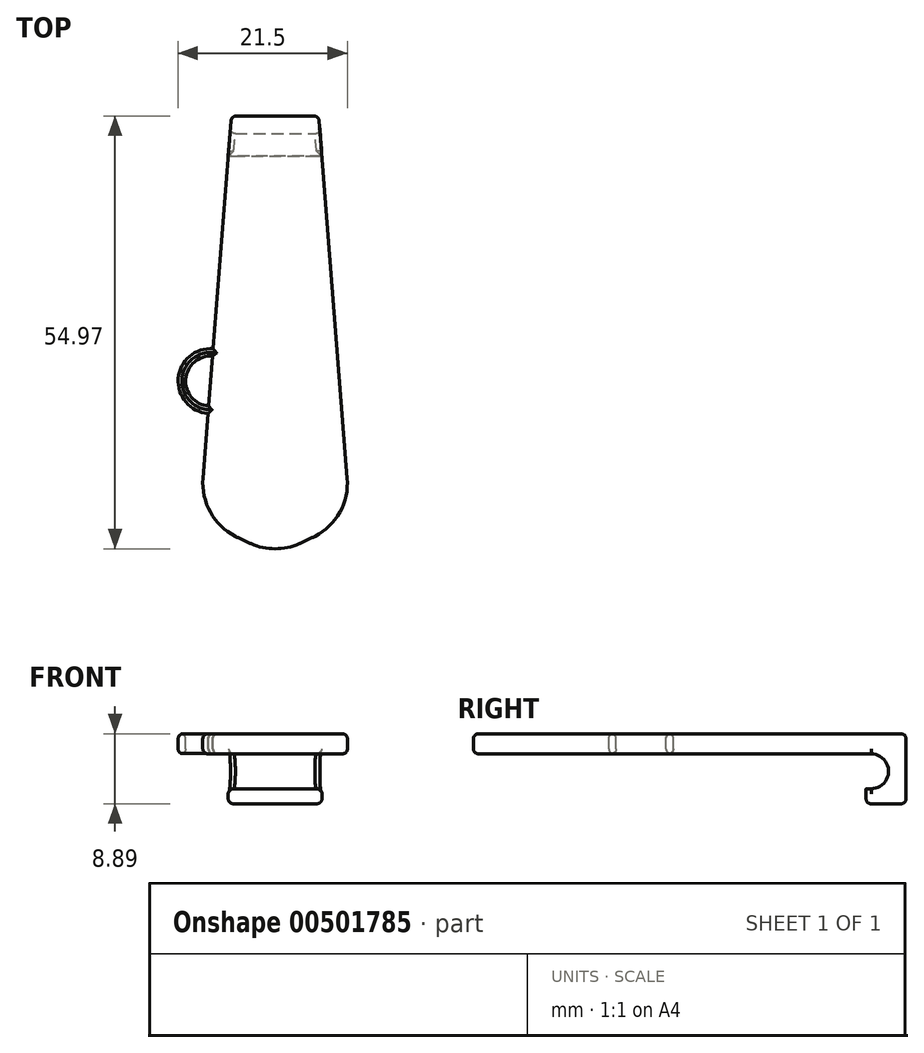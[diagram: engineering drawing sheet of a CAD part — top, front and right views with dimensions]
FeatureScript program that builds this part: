
annotation { "Feature Type Name" : "Feature", "Feature Type Description" : "" }
export const myFeature = defineFeature(function(context is Context, id is Id, definition is map)
    precondition{}
    {
        {
            var Q0;
            Q0=qCreatedBy(makeId("Top.planeOp"),FACE);
            var sketch = newSketch(context, id + "F0", { "sketchPlane" : qUnion([Q0])});
            skLineSegment(sketch, "E0", {"start": v(-9.52, -20.54) * mm, "end": v(-5.56, 30.1) * mm});
            skLineSegment(sketch, "E1", {"start": v(-5.56, 30.1) * mm, "end": v(0, 30.1) * mm});
            skArc(sketch, "E2", {"start": v(-9.52, -20.54) * mm, "mid": v(-4.94, -23.32) * mm, "end": v(0, -25.4) * mm});
            skLineSegment(sketch, "E3", {"start": v(0, 30.1) * mm, "end": v(0, -25.4) * mm});
            skSolve(sketch);
        }
        {
            var Q0;
            Q0=makeQuery(id+"F0.imprint","IMPRINT",FACE,{"disambiguationData":[TD([[makeQuery(id+"F0.imprint","IMPRINT",EDGE,{"derivedFrom":sQuery(id+"F0.wireOp",EDGE,"E0")}),-1.0]])]});
            extrude(context, id + "F1", {"entities" : qUnion([Q0]), "depth" : 2.54 * mm});
        }
        {
            var Q0;
            Q0=makeQuery(id+"F1.opExtrude","SWEPT_BODY",BODY,{"disambiguationData":[OSD([sQuery(id+"F0.wireOp",EDGE,"E0"),sQuery(id+"F0.wireOp",EDGE,"E1"),sQuery(id+"F0.wireOp",EDGE,"E2"),sQuery(id+"F0.wireOp",EDGE,"E3")])]});
            var Q1;
            Q1=qCreatedBy(makeId("Right.planeOp"),FACE);
            mirror(context, id + "F2", {"operationType" : NewBodyOperationType.ADD, "entities" : qUnion([Q0]), "mirrorPlane" : qUnion([Q1])});
        }
        {
            var Q0;
            {var subQ0=makeQuery(id+"F1.opExtrude","CAP_FACE",FACE,{"disambiguationData":[OSD([sQuery(id+"F0.wireOp",EDGE,"E0"),sQuery(id+"F0.wireOp",EDGE,"E1"),sQuery(id+"F0.wireOp",EDGE,"E2"),sQuery(id+"F0.wireOp",EDGE,"E3")])],"isStart":true});Q0=makeQuery(id+"F2.boolean.opBoolean","MERGE",FACE,{"derivedFrom":[subQ0,makeQuery(id+"F2.opPattern","COPY",FACE,{"derivedFrom":subQ0,"instanceName":"1"})]});}
            var sketch = newSketch(context, id + "F3", { "sketchPlane" : qUnion([Q0])});
            skLineSegment(sketch, "E4.0", {"start": v(-5.56, -30.1) * mm, "end": v(5.56, -30.1) * mm});
            skLineSegment(sketch, "E5.0", {"start": v(9.52, 20.54) * mm, "end": v(5.56, -30.1) * mm});
            skLineSegment(sketch, "E6.0", {"start": v(-9.52, 20.54) * mm, "end": v(-5.56, -30.1) * mm});
            skLineSegment(sketch, "E7", {"start": v(5.95, -25.03) * mm, "end": v(-5.95, -25.03) * mm});
            skSolve(sketch);
        }
        {
            var Q0;
            {var subQ0=sQuery(id+"F3.wireOp",EDGE,"E4.0");Q0=makeQuery(id+"F3.imprint","IMPRINT",FACE,{"disambiguationData":[TD([[makeQuery(id+"F3.imprint","IMPRINT",EDGE,{"derivedFrom":subQ0}),1.0]])]});}
            extrude(context, id + "F4", {"entities" : qUnion([Q0]), "operationType" : NewBodyOperationType.ADD, "depth" : 6.35 * mm});
        }
        {
            var Q0;
            Q0=qCreatedBy(makeId("Right.planeOp"),FACE);
            var sketch = newSketch(context, id + "F5", { "sketchPlane" : qUnion([Q0])});
            skPoint(sketch, "E8.0", {"position": v(25.03, 0) * mm});
            skLineSegment(sketch, "E9", {"start": v(25.03, 0) * mm, "end": v(25.66, 0) * mm});
            skLineSegment(sketch, "E10", {"start": v(25.03, -4.45) * mm, "end": v(25.66, -4.45) * mm});
            skArc(sketch, "E11", {"start": v(25.66, -4.45) * mm, "mid": v(27.88, -2.22) * mm, "end": v(25.66, 0) * mm});
            skLineSegment(sketch, "E12", {"start": v(25.03, 0) * mm, "end": v(25.03, -4.45) * mm});
            skSolve(sketch);
        }
        {
            var Q0;
            Q0 = qSketchRegion(id + "F5", true);
            extrude(context, id + "F6", {"entities" : qUnion([Q0]), "operationType" : NewBodyOperationType.REMOVE, "endBound" : BoundingType.SYMMETRIC, "oppositeDirection" : true, "depth" : 25.4 * mm});
        }
        {
            var Q0;
            {var subQ0=makeQuery(id+"F1.opExtrude","CAP_FACE",FACE,{"disambiguationData":[OSD([sQuery(id+"F0.wireOp",EDGE,"E0"),sQuery(id+"F0.wireOp",EDGE,"E1"),sQuery(id+"F0.wireOp",EDGE,"E2"),sQuery(id+"F0.wireOp",EDGE,"E3")])],"isStart":false});Q0=makeQuery(id+"F2.boolean.opBoolean","MERGE",FACE,{"derivedFrom":[subQ0,makeQuery(id+"F2.opPattern","COPY",FACE,{"derivedFrom":subQ0,"instanceName":"1"})]});}
            var sketch = newSketch(context, id + "F7", { "sketchPlane" : qUnion([Q0])});
            skCircle(sketch, "E13", {"center": v(-8.2, -3.55) * mm, "radius": 4.13 * mm});
            skCircle(sketch, "E14", {"center": v(-8.2, -3.55) * mm, "radius": 3.18 * mm});
            skCircle(sketch, "E15.MirrorC", {"center": v(8.2, -3.55) * mm, "radius": 3.18 * mm});
            skCircle(sketch, "E16.MirrorC", {"center": v(8.2, -3.55) * mm, "radius": 4.13 * mm});
            skSolve(sketch);
        }
        {
            var Q0;
            {var subQ0=sQuery(id+"F7.wireOp",EDGE,"E13");var subQ1=makeQuery(id+"F1.opExtrude","CAP_EDGE",EDGE,{"disambiguationData":[OSD([sQuery(id+"F0.wireOp",EDGE,"E0")])],"isStart":false});var subQ2=makeQuery(id+"F7.imprint","INTERSECT",VERTEX,{"disambiguationData":[OD(0.0)],"derivedFrom":[subQ1,subQ0]});Q0=makeQuery(id+"F7.imprint","IMPRINT",FACE,{"disambiguationData":[TD([[makeQuery(id+"F7.imprint","IMPRINT",EDGE,{"disambiguationData":[TD([[subQ2,1.0]])],"derivedFrom":subQ0}),1.0]])]});}
            var Q1;
            {var subQ0=sQuery(id+"F7.wireOp",EDGE,"E15.MirrorC");var subQ1=makeQuery(id+"F2.opPattern","COPY",EDGE,{"derivedFrom":makeQuery(id+"F1.opExtrude","CAP_EDGE",EDGE,{"disambiguationData":[OSD([sQuery(id+"F0.wireOp",EDGE,"E0")])],"isStart":false}),"instanceName":"1"});var subQ2=makeQuery(id+"F7.imprint","INTERSECT",VERTEX,{"disambiguationData":[OD(0.0)],"derivedFrom":[subQ1,subQ0]});Q1=makeQuery(id+"F7.imprint","IMPRINT",FACE,{"disambiguationData":[TD([[makeQuery(id+"F7.imprint","IMPRINT",EDGE,{"disambiguationData":[TD([[subQ2,1.0]])],"derivedFrom":subQ0}),1.0]])]});}
            var Q2;
            {var subQ0=makeQuery(id+"F1.opExtrude","CAP_FACE",FACE,{"disambiguationData":[OSD([sQuery(id+"F0.wireOp",EDGE,"E0"),sQuery(id+"F0.wireOp",EDGE,"E1"),sQuery(id+"F0.wireOp",EDGE,"E2"),sQuery(id+"F0.wireOp",EDGE,"E3")])],"isStart":true});Q2=makeQuery(id+"F6.boolean.opBoolean","MERGE",FACE,{"derivedFrom":[makeQuery(id+"F2.boolean.opBoolean","MERGE",FACE,{"derivedFrom":[subQ0,makeQuery(id+"F2.opPattern","COPY",FACE,{"derivedFrom":subQ0,"instanceName":"1"})]}),makeQuery(id+"F6.opExtrude","SWEPT_FACE",FACE,{"disambiguationData":[OSD([sQuery(id+"F5.wireOp",EDGE,"E9")])]})]});}
            extrude(context, id + "F8", {"entities" : qUnion([Q0, Q1]), "operationType" : NewBodyOperationType.ADD, "endBound" : BoundingType.UP_TO_SURFACE, "oppositeDirection" : true, "endBoundEntityFace" : qUnion([Q2]), "depth" : 25.4 * mm});
        }
        {
            var Q0;
            Q0=makeQuery(id+"F2.opPattern","COPY",EDGE,{"derivedFrom":makeQuery(id+"F1.opExtrude","SWEPT_EDGE",EDGE,{"disambiguationData":[OSD([sQuery(id+"F0.wireOp",EDGE,"E0"),sQuery(id+"F0.wireOp",EDGE,"E2")])]}),"instanceName":"1"});
            var Q1;
            {var subQ0=makeQuery(id+"F1.opExtrude","SWEPT_EDGE",EDGE,{"disambiguationData":[OSD([sQuery(id+"F0.wireOp",EDGE,"E2"),sQuery(id+"F0.wireOp",EDGE,"E3")])]});Q1=makeQuery(id+"F2.boolean.opBoolean","MERGE",EDGE,{"derivedFrom":[subQ0,makeQuery(id+"F2.opPattern","COPY",EDGE,{"derivedFrom":subQ0,"instanceName":"1"})]});}
            var Q2;
            Q2=makeQuery(id+"F1.opExtrude","SWEPT_EDGE",EDGE,{"disambiguationData":[OSD([sQuery(id+"F0.wireOp",EDGE,"E0"),sQuery(id+"F0.wireOp",EDGE,"E2")])]});
            fillet(context, id + "F9", {"entities" : qUnion([Q0, Q1, Q2]), "radius" : 7.62 * mm, "tangentPropagation" : true, "allowEdgeOverflow" : false});
        }
        {
            var Q0;
            Q0=makeQuery(id+"F4.opExtrude","CAP_FACE",FACE,{"disambiguationData":[OSD([sQuery(id+"F3.wireOp",EDGE,"E4.0"),sQuery(id+"F3.wireOp",EDGE,"E5.0"),sQuery(id+"F3.wireOp",EDGE,"E6.0"),sQuery(id+"F3.wireOp",EDGE,"E7")])],"isStart":false});
            var Q1;
            {var subQ0=makeQuery(id+"F1.opExtrude","SWEPT_FACE",FACE,{"disambiguationData":[OSD([sQuery(id+"F0.wireOp",EDGE,"E1")])]});Q1=makeQuery(id+"F4.boolean.opBoolean","MERGE",FACE,{"derivedFrom":[makeQuery(id+"F2.boolean.opBoolean","MERGE",FACE,{"derivedFrom":[subQ0,makeQuery(id+"F2.opPattern","COPY",FACE,{"derivedFrom":subQ0,"instanceName":"1"})]}),makeQuery(id+"F4.opExtrude","SWEPT_FACE",FACE,{"disambiguationData":[OSD([sQuery(id+"F3.wireOp",EDGE,"E4.0")])]})]});}
            var Q2;
            {var subQ0=sQuery(id+"F7.wireOp",EDGE,"E15.MirrorC");var subQ1=sQuery(id+"F0.wireOp",EDGE,"E0");var subQ2=makeQuery(id+"F1.opExtrude","CAP_EDGE",EDGE,{"disambiguationData":[OSD([subQ1])],"isStart":false});var subQ3=makeQuery(id+"F2.opPattern","COPY",EDGE,{"derivedFrom":subQ2,"instanceName":"1"});var subQ4=sQuery(id+"F5.wireOp",EDGE,"E9");var subQ5=sQuery(id+"F0.wireOp",EDGE,"E3");var subQ6=sQuery(id+"F0.wireOp",EDGE,"E2");var subQ7=sQuery(id+"F0.wireOp",EDGE,"E1");var subQ8=sQuery(id+"F7.wireOp",EDGE,"E13");var subQ9=makeQuery(id+"F1.opExtrude","CAP_FACE",FACE,{"disambiguationData":[OSD([subQ1,subQ7,subQ6,subQ5])],"isStart":true});Q2=makeQuery(id+"F8.boolean.opBoolean","MERGE",FACE,{"derivedFrom":[makeQuery(id+"F6.boolean.opBoolean","MERGE",FACE,{"derivedFrom":[makeQuery(id+"F2.boolean.opBoolean","MERGE",FACE,{"derivedFrom":[subQ9,makeQuery(id+"F2.opPattern","COPY",FACE,{"derivedFrom":subQ9,"instanceName":"1"})]}),makeQuery(id+"F6.opExtrude","SWEPT_FACE",FACE,{"disambiguationData":[OSD([subQ4])]})]}),makeQuery(id+"F8.opExtrude","CAP_FACE",FACE,{"disambiguationData":[OSD([subQ1,subQ7,subQ6,subQ5,subQ4]),ownerDisambiguation([makeQuery(id+"F7.imprint","IMPRINT",EDGE,{"disambiguationData":[TD([[makeQuery(id+"F7.imprint","INTERSECT",VERTEX,{"disambiguationData":[OD(0.0)],"derivedFrom":[subQ2,subQ8]}),1.0]])],"derivedFrom":subQ8})])],"isStart":false}),makeQuery(id+"F8.opExtrude","CAP_FACE",FACE,{"disambiguationData":[OSD([subQ1,subQ7,subQ6,subQ5,subQ4]),ownerDisambiguation([makeQuery(id+"F7.imprint","IMPRINT",EDGE,{"disambiguationData":[TD([[makeQuery(id+"F7.imprint","INTERSECT",VERTEX,{"disambiguationData":[OD(0.0)],"derivedFrom":[subQ3,subQ0]}),1.0]])],"derivedFrom":subQ0})])],"isStart":false})]});}
            var Q3;
            Q3=makeQuery(id+"F6.boolean.opBoolean","COPY",FACE,{"derivedFrom":makeQuery(id+"F6.opExtrude","SWEPT_FACE",FACE,{"disambiguationData":[OSD([sQuery(id+"F5.wireOp",EDGE,"E11")])]})});
            var Q4;
            {var subQ0=sQuery(id+"F0.wireOp",EDGE,"E0");var subQ1=makeQuery(id+"F1.opExtrude","CAP_FACE",FACE,{"disambiguationData":[OSD([subQ0,sQuery(id+"F0.wireOp",EDGE,"E1"),sQuery(id+"F0.wireOp",EDGE,"E2"),sQuery(id+"F0.wireOp",EDGE,"E3")])],"isStart":false});Q4=makeQuery(id+"F8.boolean.opBoolean","MERGE",FACE,{"derivedFrom":[makeQuery(id+"F2.boolean.opBoolean","MERGE",FACE,{"derivedFrom":[subQ1,makeQuery(id+"F2.opPattern","COPY",FACE,{"derivedFrom":subQ1,"instanceName":"1"})]}),makeQuery(id+"F8.opExtrude","CAP_FACE",FACE,{"disambiguationData":[OSD([subQ0,sQuery(id+"F7.wireOp",EDGE,"E13"),sQuery(id+"F7.wireOp",EDGE,"E14")])],"isStart":true}),makeQuery(id+"F8.opExtrude","CAP_FACE",FACE,{"disambiguationData":[OSD([subQ0,sQuery(id+"F7.wireOp",EDGE,"E15.MirrorC"),sQuery(id+"F7.wireOp",EDGE,"E16.MirrorC")])],"isStart":true})]});}
            fillet(context, id + "F10", {"entities" : qUnion([Q0, Q1, Q2, Q3, Q4]), "radius" : 0.64 * mm, "tangentPropagation" : true, "allowEdgeOverflow" : false});
        }
    });
